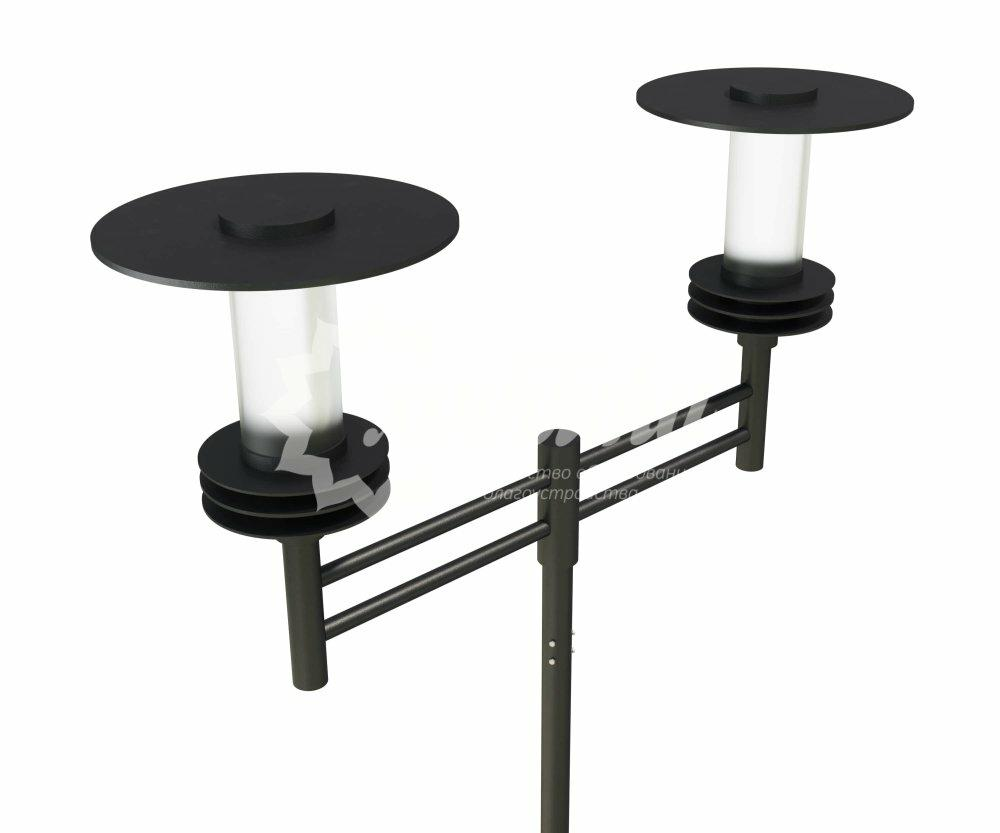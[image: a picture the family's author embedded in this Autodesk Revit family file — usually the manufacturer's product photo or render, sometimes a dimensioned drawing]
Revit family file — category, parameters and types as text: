
# Revit family: 9850 Уличный фонарь «Техно - 2» Хоббика
name_source: partatom
category: Антураж
revit_build: Autodesk Revit 2018 (Build: 20180423_1000(x64)
units: mm (PartAtom-declared; Revit-internal decimal feet)

## family parameters
Всегда вертикально = Да
Источник визуального образа = Геометрия семейства
На основе рабочей плоскости = Нет
Общий = Нет
При загрузке вырезать с полостями = Нет
Точка расчета площади = Нет

## types (3) — shared parameters
URL = https://hobbyka.ru
Артикул товара = Арт. 9850
Группа модели = Светильники со стальными опорами
Длина = 1624 мм
Изготовитель = ООО «Хоббика»
Изображение типоразмера = Уличный фонарь «Техно - 2» Арт 9850.jpg
Материал изделия = Сталь
Цвет каркаса = Сталь
Ширина = 511 мм

## per-type parameters (varying)
| type | Версия 4,0 м | Версия 4,5 м | Версия 5,0 м | Высота | Описание |
| Версия 4,0 м | Да | Нет | Нет | 4000 мм | Уличный фонарь «Техно - 2». Версия 4,0 м |
| Версия 4,5 м | Нет | Да | Нет | 4500 мм | Уличный фонарь «Техно - 2». Версия 4,5 м |
| Версия 5,0 м | Нет | Нет | Да | 5000 мм | Уличный фонарь «Техно - 2». Версия 5,0 м |
